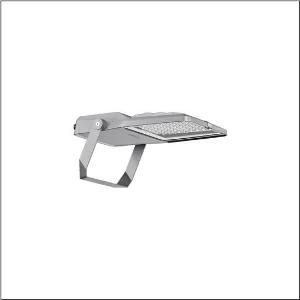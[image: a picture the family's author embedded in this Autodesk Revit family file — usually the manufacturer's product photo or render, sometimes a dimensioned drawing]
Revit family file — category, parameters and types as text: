
# Revit family: floodlight_fl_21_mini___pl61_5xa7773c2c1a_b950
name_source: partatom
category: Lighting Fixtures
units: mm (PartAtom-declared; Revit-internal decimal feet)

## family parameters
Cut with Voids When Loaded = No
Host = Face
Light Source = No
Part Type = Normal
Room Calculation Point = No
Round Connector Dimension = Use Diameter
Shared = No

## types (1)
- --- (1 x LED, 19150 lm, 163.5 W, 3000K)
    Apparent Load = 163 VA
    CIE Flux Codes = 33 65 98 100 100
    Color Rendering = 70
    Color Temperature = 3000K
    Default Elevation = 1800 mm
    Description = Floodlight FL 21 mini, floodlight, primary light control with lens, of PMMA, primary optical cover: protective disc, of toughened safety glass, transparent, light distribution: PL61, light emission: direct distribution, installation type: surface-mounted, LED, High Power LED, rated luminous flux: 19.150lm, luminous efficacy: 117lm/W, light colour: 730, colour temperature: 3000K, control gear: ON/OFF Multilumen, control: pre-setting: linear dimming characteristic, Temp-Guard, with terminal, 6-pole, mains connection: 220..240V, AC, 50/60Hz, start of lifetime: 164W, luminaire housing, of diecast aluminium, powder-coated, SITECO metallic grey (DB 702S), corrosivity category C5 mid according to DIN EN ISO 12944, suitable for swimming pools, chlorine-resistant, sealing non-destructively replaceable, mounting bracket, of steel, galvanised, powder-coated, SITECO metallic grey (DB 702S), ON/OFF, protection rating (complete): IP66, insulation class (complete): insulation class I (protective earthing), certification: CE, ENEC, VDE, protection symbol: D, impact resistance: IK08, permissible operating ambient temperature: -40..+40°C, permissible operating ambient temperature for outdoor applications: -40..+50°C, standard: DIN EN 12944, LABS conformity tested according to VDMA 24364:2018-05, packaging unit: 1 piece

Light Distribution: PL61
    Height = 70 mm
    Lamp = 1 x LED
    Lamp Light Flux = 19150 lm
    Lamp Power = 163.5 W
    Lamp count = 1
    Length = 485 mm
    Luminous efficacy = 117 lm/W
    Manufacturer = Siteco
    ModVariant = No
    Model = 5XA7773C2C1A
    Mounting Place = Pole
    Mounting Type = Pole annexe
    Number of Poles = 1
    OnlyDefault = Yes
    Power Factor = 1
    Product Name = Floodlight FL 21 mini | PL61
    Product group = floodlight | pylon annexe
    ProductGroupID = 6201
    Protection Class = Protection class I
    Protection Degree = IP 66
    RLX_Detail_Level = 1
    RLX_Emergency_Light_Flux = 0 lm
    RLX_Emergency_Type = 0
    RLX_Emergency_Type_DB = No
    RlxData = <blob elided: 94453 chars, md5=cd65c2c1>
    Socket = socket
    Standby Power = 0 W
    System Light Flux = 19150 lm
    System Power = 163 W
    Type Comments = factory setting: luminous flux: 100 % | (ON | - | - | - | - | - | - | -) | 825 mA
    Type Image = l_1006845.jpg
    URL = http://relux.com
    VarID = @adj_173889
    Voltage = 0 V
    Weight = 0.00 kg
    Width = 337 mm

## geometry (parser evidence)
native form markers: Blend x4, Sweep x14
no freeform markers — native parametric forms only
